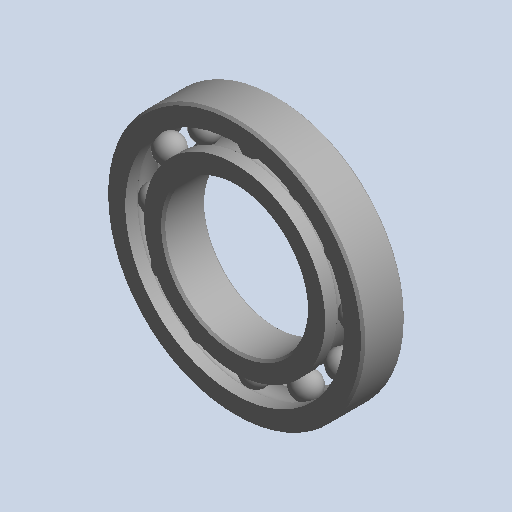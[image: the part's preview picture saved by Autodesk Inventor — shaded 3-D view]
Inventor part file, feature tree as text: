
AUTODESK INVENTOR PART (.ipt)
format: ipt  version: 2022.3 (Build 263350000, 350)  size: 535,040 bytes
history: native  units: mm (DEFAULTED — no unit token found)
features: other x11, revolve x3
ambient origin geometry x8: Origin, YZ Plane, XZ Plane, XY Plane, X Axis, Y Axis, Z Axis, Center Point
bodies: Solid1 (feature_tree), Solid2 (feature_tree), Solid3 (feature_tree), Solid4 (feature_tree), Solid5 (feature_tree), Solid6 (feature_tree), Solid7 (feature_tree), Solid8 (feature_tree), Solid9 (feature_tree), Solid10 (feature_tree), Solid11 (feature_tree), Solid12 (feature_tree), Solid13 (feature_tree), Solid14 (feature_tree)
feature tree (14):
  revolve  "Revolve1"  [1 undecoded]
  revolve  "Revolve3"  [1 undecoded]
  revolve  "Revolve4"  [1 undecoded]
  other  "CirPattern1[1]"
  other  "CirPattern1[2]"
  other  "CirPattern1[3]"
  other  "CirPattern1[4]"
  other  "CirPattern1[5]"
  other  "CirPattern1[6]"
  other  "CirPattern1[7]"
  other  "CirPattern1[8]"
  other  "CirPattern1[9]"
  other  "CirPattern1[10]"
  other  "CirPattern1[11]"
note: 3 required parameter values undecoded (feature->parameter linkage not recoverable at this tier; creation-order binding heuristic only, values carry confidence <= 0.55)
